# Revit family: Seating_Inc-Kudl-Chair-Wood
name_source: partatom
category: Furniture
revit_build: Autodesk Revit MEP 2014 (Build: 20130308_1515(x64)
units: mm (PartAtom-declared; Revit-internal decimal feet)

## types (4) — shared parameters
Assembly Code = E2020200
Depth = 26"
Keynote = 12500
Leg = STI - Wood
Manufacturer = seating inc.
Seat = STI - Fabric
Type Comments = Kudl
URL = http://www.seatinginc.com
Width = 25"

## per-type parameters (varying)
| type | Description | Full Back | Height | Leg Rest | Leg Support | Model | Open Back |
| Kudl 4-Leg Wood KF4W | Kudl 4-Leg Wood 25"W 26"D 33.5"H | Yes | 33 1/2" | No | 24 101/128" | KF4W | No |
| Kudl 4-Leg Wood Tall KF4T | Kudl 4-Leg Wood Tall 25"W 26"D 40.5"H | Yes | 40 1/2" | Yes | 27 179/256" | KF4T | No |
| Kudl 4-Leg Wood KO4W | Kudl 4-Leg Wood 25"W 26"D 33.5"H | No | 33 1/2" | No | 24 101/128" | KO4W | Yes |
| Kudl 4-Leg Wood Tall KO4T | Kudl 4-Leg Wood Tall 25"W 26"D 40.5"H | No | 40 1/2" | Yes | 27 179/256" | KO4T | Yes |

## geometry (parser evidence)
native form markers: Sweep x1
no freeform markers — native parametric forms only
